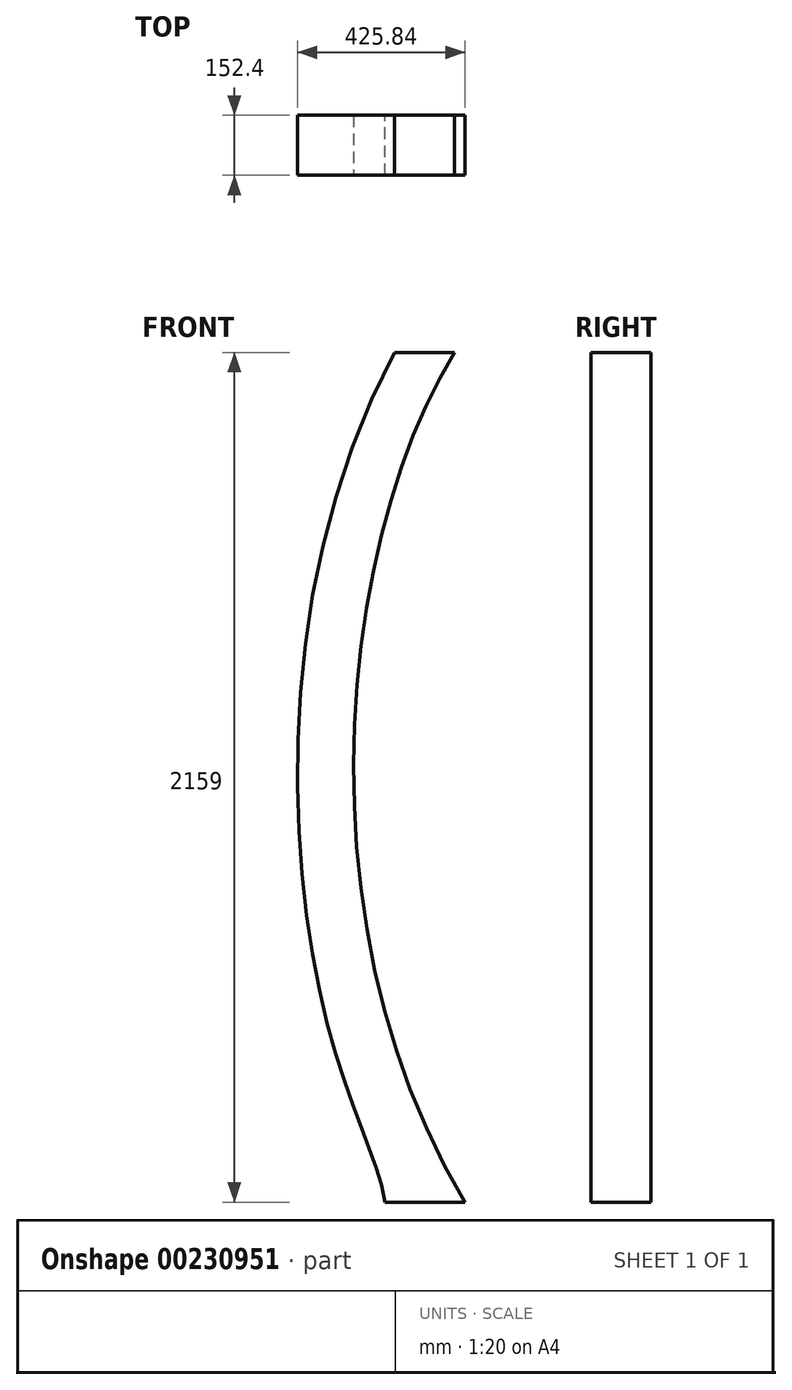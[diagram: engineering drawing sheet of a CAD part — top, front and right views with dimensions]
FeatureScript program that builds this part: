
annotation { "Feature Type Name" : "Feature", "Feature Type Description" : "" }
export const myFeature = defineFeature(function(context is Context, id is Id, definition is map)
    precondition{}
    {
        {
            var Q0;
            Q0=qCreatedBy(makeId("Front.planeOp"),FACE);
            var sketch = newSketch(context, id + "F0", { "sketchPlane" : qUnion([Q0])});
            skLineSegment(sketch, "E0", {"start": v(0, -1193.8) * mm, "end": v(-919.23, -1193.8) * mm});
            skLineSegment(sketch, "E1", {"start": v(0, 965.2) * mm, "end": v(-945.58, 965.2) * mm});
            skFitSpline(sketch, "E2", {"points": [v(-945.58, 965.2) * mm, v(-919.23, -1193.8) * mm], "startDerivative": vector(-889.45, -1441.33) * mm, "endDerivative": vector(1263.87, -2098.17) * mm});
            skLineSegment(sketch, "E3", {"start": v(-945.58, 965.2) * mm, "end": v(-1097.98, 965.2) * mm});
            skLineSegment(sketch, "E4", {"start": v(-919.23, -1193.8) * mm, "end": v(-1122.43, -1193.8) * mm});
            skFitSpline(sketch, "E5", {"points": [v(-1097.98, 965.2) * mm, v(-1266.7, -749.28) * mm, v(-1122.43, -1193.8) * mm], "startDerivative": vector(-1456.54, -2733.7) * mm, "endDerivative": vector(159.23, -982.95) * mm});
            skSolve(sketch);
        }
        {
            var Q0;
            Q0=qSketchRegion(id+"F0",true);
            extrude(context, id + "F1", {"entities" : qUnion([Q0]), "endBound" : BoundingType.SYMMETRIC, "depth" : 152.4 * mm});
        }
    });
